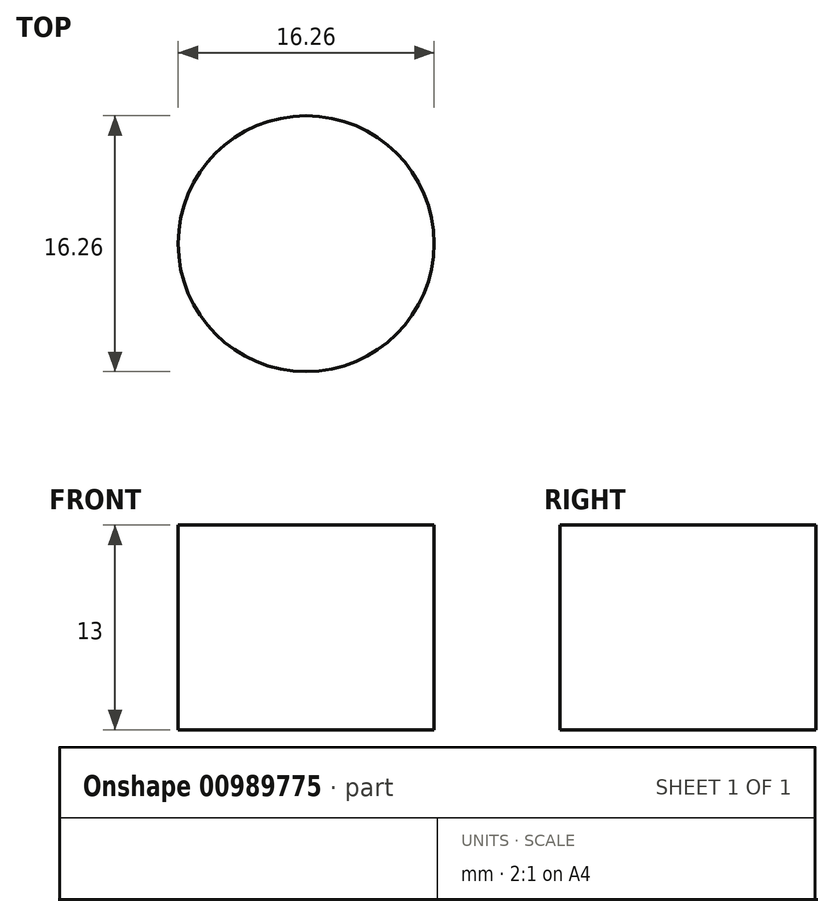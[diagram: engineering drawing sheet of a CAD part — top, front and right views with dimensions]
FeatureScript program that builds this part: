
annotation { "Feature Type Name" : "Feature", "Feature Type Description" : "" }
export const myFeature = defineFeature(function(context is Context, id is Id, definition is map)
    precondition{}
    {
        {
            var Q0;
            Q0=qCreatedBy(makeId("Top.planeOp"),FACE);
            var sketch = newSketch(context, id + "F0", { "sketchPlane" : qUnion([Q0])});
            skCircle(sketch, "E0", {"center": v(0, 0) * mm, "radius": 8.13 * mm});
            skSolve(sketch);
        }
        {
            var Q0;
            Q0 = qSketchRegion(id + "F0", true);
            extrude(context, id + "F1", {"entities" : qUnion([Q0]), "depth" : 13 * mm, "offsetDistance" : 25 * mm});
        }
    });
